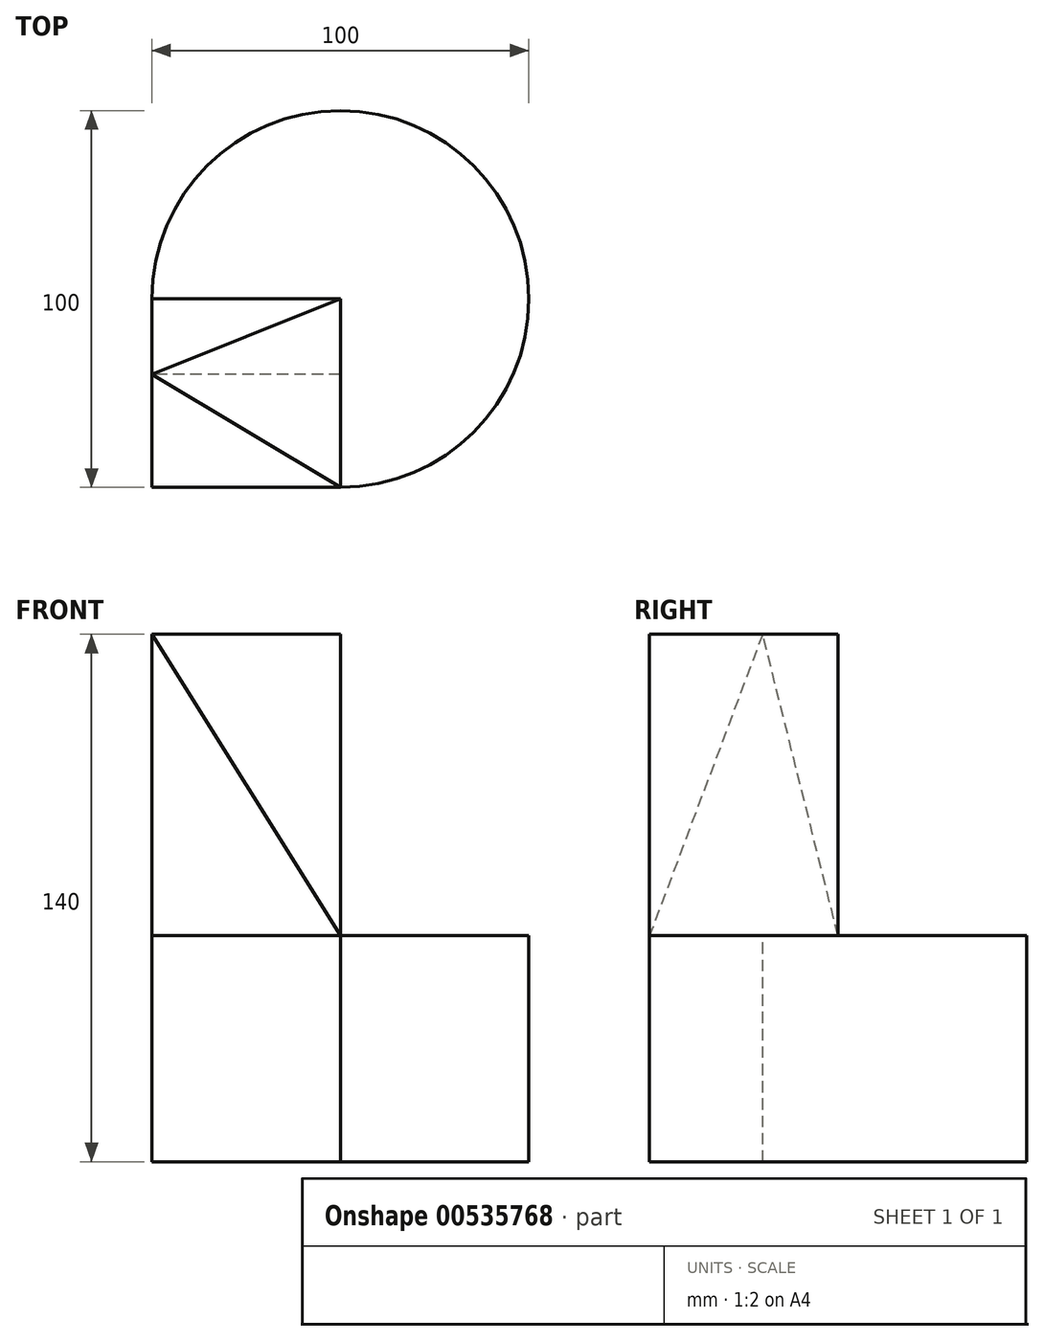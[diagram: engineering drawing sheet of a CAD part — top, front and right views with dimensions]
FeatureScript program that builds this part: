
annotation { "Feature Type Name" : "Feature", "Feature Type Description" : "" }
export const myFeature = defineFeature(function(context is Context, id is Id, definition is map)
    precondition{}
    {
        {
            var Q0;
            Q0=qCreatedBy(makeId("Top.planeOp"),FACE);
            var sketch = newSketch(context, id + "F0", { "sketchPlane" : qUnion([Q0])});
            skCircle(sketch, "E0", {"center": v(0, 0) * mm, "radius": 50 * mm});
            skSolve(sketch);
        }
        {
            var Q0;
            Q0 = qSketchRegion(id + "F0", true);
            extrude(context, id + "F1", {"entities" : qUnion([Q0]), "depth" : 60 * mm, "offsetDistance" : 25 * mm});
        }
        {
            var Q0;
            Q0=makeQuery(id+"F1.opExtrude","CAP_FACE",FACE,{"disambiguationData":[OSD([sQuery(id+"F0.wireOp",EDGE,"E0")])],"isStart":false});
            var sketch = newSketch(context, id + "F2", { "sketchPlane" : qUnion([Q0])});
            skArc(sketch, "E1", {"start": v(-50, 0) * mm, "mid": v(-35.36, -35.36) * mm, "end": v(0, -50) * mm});
            skLineSegment(sketch, "E2", {"start": v(-50, 0) * mm, "end": v(0, 0) * mm});
            skLineSegment(sketch, "E3", {"start": v(0, -50) * mm, "end": v(0, 0) * mm});
            skSolve(sketch);
        }
        {
            var Q0;
            Q0 = qSketchRegion(id + "F2", true);
            extrude(context, id + "F3", {"entities" : qUnion([Q0]), "operationType" : NewBodyOperationType.REMOVE, "endBound" : BoundingType.UP_TO_NEXT, "oppositeDirection" : true, "depth" : 25 * mm, "offsetDistance" : 25 * mm});
        }
        {
            var Q0;
            Q0=qCreatedBy(makeId("Top.planeOp"),FACE);
            var sketch = newSketch(context, id + "F4", { "sketchPlane" : qUnion([Q0])});
            skLineSegment(sketch, "E4.bottom", {"start": v(0, 0) * mm, "end": v(-50, 0) * mm});
            skLineSegment(sketch, "E4.top", {"start": v(0, -50) * mm, "end": v(-50, -50) * mm});
            skLineSegment(sketch, "E4.left", {"start": v(0, 0) * mm, "end": v(0, -50) * mm});
            skLineSegment(sketch, "E4.right", {"start": v(-50, 0) * mm, "end": v(-50, -50) * mm});
            skSolve(sketch);
        }
        {
            var Q0;
            Q0 = qSketchRegion(id + "F4", true);
            extrude(context, id + "F5", {"entities" : qUnion([Q0]), "operationType" : NewBodyOperationType.ADD, "depth" : 140 * mm, "offsetDistance" : 25 * mm});
        }
        {
            var Q0;
            Q0=makeQuery(id+"F5.opExtrude","SWEPT_FACE",FACE,{"disambiguationData":[OSD([sQuery(id+"F4.wireOp",EDGE,"E4.right")])]});
            var sketch = newSketch(context, id + "F6", { "sketchPlane" : qUnion([Q0])});
            skLineSegment(sketch, "E5", {"start": v(50, 0) * mm, "end": v(20, 0) * mm});
            skLineSegment(sketch, "E6", {"start": v(20, 0) * mm, "end": v(20, 60) * mm});
            skLineSegment(sketch, "E7", {"start": v(20, 60) * mm, "end": v(50, 60) * mm});
            skSolve(sketch);
        }
        {
            var Q0;
            Q0 = qSketchRegion(id + "F6", true);
            var Q1;
            {var subQ0=sQuery(id+"F6.wireOp",EDGE,"E5");Q1=makeQuery(id+"F6.imprint","IMPRINT",FACE,{"disambiguationData":[TD([[makeQuery(id+"F6.imprint","IMPRINT",EDGE,{"derivedFrom":subQ0}),1.0]])]});}
            extrude(context, id + "F7", {"entities" : qUnion([Q0, Q1]), "operationType" : NewBodyOperationType.REMOVE, "oppositeDirection" : true, "depth" : 50 * mm, "offsetDistance" : 25 * mm});
        }
        {
            var Q0;
            Q0=makeQuery(id+"F5.opExtrude","CAP_FACE",FACE,{"disambiguationData":[OSD([sQuery(id+"F4.wireOp",EDGE,"E4.bottom"),sQuery(id+"F4.wireOp",EDGE,"E4.top"),sQuery(id+"F4.wireOp",EDGE,"E4.left"),sQuery(id+"F4.wireOp",EDGE,"E4.right")])],"isStart":false});
            var sketch = newSketch(context, id + "F8", { "sketchPlane" : qUnion([Q0])});
            skLineSegment(sketch, "E8", {"start": v(-50, -50) * mm, "end": v(-50, -20) * mm});
            skSolve(sketch);
        }
        {
            var Q0;
            Q0=sQuery(id+"F8.wireOp",VERTEX,"E8.end");
            var Q1;
            Q1=makeQuery(id+"F7.boolean.opBoolean","COPY",VERTEX,{"derivedFrom":makeQuery(id+"F7.opExtrude","CAP_VERTEX",VERTEX,{"disambiguationData":[OSD([sQuery(id+"F4.wireOp",EDGE,"E4.top"),sQuery(id+"F4.wireOp",EDGE,"E4.right"),sQuery(id+"F6.wireOp",EDGE,"E7")])],"isStart":true})});
            var Q2;
            Q2=makeQuery(id+"F3.boolean.opBoolean","COPY",VERTEX,{"derivedFrom":makeQuery(id+"F3.opExtrude","CAP_VERTEX",VERTEX,{"disambiguationData":[OSD([sQuery(id+"F0.wireOp",EDGE,"E0"),sQuery(id+"F2.wireOp",EDGE,"E1"),sQuery(id+"F2.wireOp",EDGE,"E3")])],"isStart":true})});
            cPlane(context, id + "F9", {"entities" : qUnion([Q0, Q1, Q2]), "cplaneType" : CPlaneType.THREE_POINT, "offset" : 25 * mm, "width" : 150 * mm, "height" : 150 * mm});
        }
        {
            var Q0;
            {var subQ1=sQuery(id+"F8.wireOp",EDGE,"E8");Q0=makeQuery(id+"F8.imprint","IMPRINT",FACE,{"disambiguationData":[TD([[makeQuery(id+"F8.imprint","IMPRINT",EDGE,{"derivedFrom":subQ1}),1.0]])]});}
            var sketch = newSketch(context, id + "F10", { "sketchPlane" : qUnion([Q0])});
            skLineSegment(sketch, "E9", {"start": v(0, -3.93) * mm, "end": v(0, -50) * mm});
            skLineSegment(sketch, "E10", {"start": v(0, -50) * mm, "end": v(-50, -50) * mm});
            skLineSegment(sketch, "E11", {"start": v(-50, -50) * mm, "end": v(-50, -20) * mm});
            skLineSegment(sketch, "E12", {"start": v(-50, -20) * mm, "end": v(0, -50) * mm});
            skSolve(sketch);
        }
        {
            var Q0;
            Q0 = qSketchRegion(id + "F10", true);
            var Q1;
            Q1=qCreatedBy(id+"F9.planeOp",FACE);
            extrude(context, id + "F11", {"entities" : qUnion([Q0]), "operationType" : NewBodyOperationType.REMOVE, "endBound" : BoundingType.UP_TO_SURFACE, "oppositeDirection" : true, "depth" : 25 * mm, "endBoundEntityFace" : qUnion([Q1]), "offsetDistance" : 25 * mm});
        }
        {
            var Q0;
            Q0=sQuery(id+"F8.wireOp",VERTEX,"E8.end");
            var Q1;
            Q1=makeQuery(id+"F3.boolean.opBoolean","COPY",VERTEX,{"derivedFrom":makeQuery(id+"F3.opExtrude","CAP_VERTEX",VERTEX,{"disambiguationData":[OSD([sQuery(id+"F2.wireOp",EDGE,"E2"),sQuery(id+"F2.wireOp",EDGE,"E3")])],"isStart":true})});
            var Q2;
            Q2=makeQuery(id+"F3.boolean.opBoolean","COPY",VERTEX,{"derivedFrom":makeQuery(id+"F3.opExtrude","CAP_VERTEX",VERTEX,{"disambiguationData":[OSD([sQuery(id+"F0.wireOp",EDGE,"E0"),sQuery(id+"F2.wireOp",EDGE,"E1"),sQuery(id+"F2.wireOp",EDGE,"E2")])],"isStart":true})});
            cPlane(context, id + "F12", {"entities" : qUnion([Q0, Q1, Q2]), "cplaneType" : CPlaneType.THREE_POINT, "offset" : 25 * mm, "width" : 150 * mm, "height" : 150 * mm});
        }
        {
            var Q0;
            {var subQ1=sQuery(id+"F8.wireOp",EDGE,"E8");Q0=makeQuery(id+"F8.imprint","IMPRINT",FACE,{"disambiguationData":[TD([[makeQuery(id+"F8.imprint","IMPRINT",EDGE,{"derivedFrom":subQ1}),1.0]])]});}
            var sketch = newSketch(context, id + "F13", { "sketchPlane" : qUnion([Q0])});
            skLineSegment(sketch, "E13", {"start": v(0, 0) * mm, "end": v(-50, 0) * mm});
            skLineSegment(sketch, "E14", {"start": v(-50, 0) * mm, "end": v(-50, -20) * mm});
            skLineSegment(sketch, "E15", {"start": v(-50, -20) * mm, "end": v(0, 0) * mm});
            skSolve(sketch);
        }
        {
            var Q0;
            Q0 = qSketchRegion(id + "F13", true);
            var Q1;
            Q1=qCreatedBy(id+"F12.planeOp",FACE);
            extrude(context, id + "F14", {"entities" : qUnion([Q0]), "operationType" : NewBodyOperationType.REMOVE, "endBound" : BoundingType.UP_TO_SURFACE, "oppositeDirection" : true, "depth" : 25 * mm, "endBoundEntityFace" : qUnion([Q1]), "offsetDistance" : 25 * mm});
        }
    });
